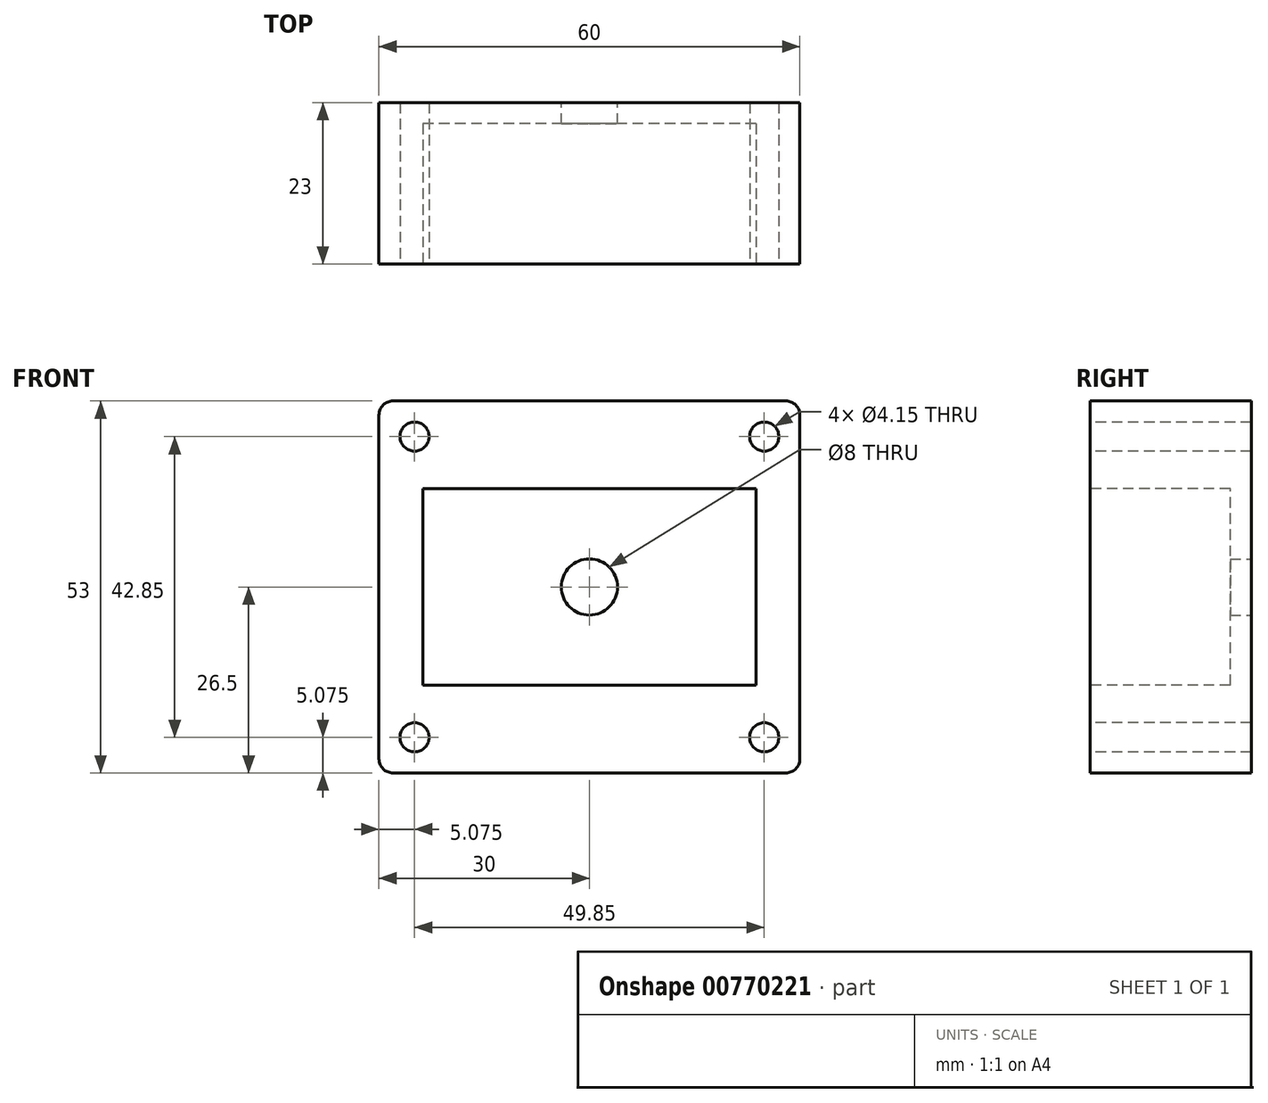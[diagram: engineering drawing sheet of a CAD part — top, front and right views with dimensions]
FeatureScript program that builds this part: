
annotation { "Feature Type Name" : "Feature", "Feature Type Description" : "" }
export const myFeature = defineFeature(function(context is Context, id is Id, definition is map)
    precondition{}
    {
        {
            var Q0;
            Q0=qCreatedBy(makeId("Front.planeOp"),FACE);
            var sketch = newSketch(context, id + "F0", { "sketchPlane" : qUnion([Q0])});
            skLineSegment(sketch, "E0.bottom", {"start": v(-30, 26.5) * mm, "end": v(30, 26.5) * mm});
            skLineSegment(sketch, "E0.top", {"start": v(-30, -26.5) * mm, "end": v(30, -26.5) * mm});
            skLineSegment(sketch, "E0.left", {"start": v(-30, 26.5) * mm, "end": v(-30, -26.5) * mm});
            skLineSegment(sketch, "E0.right", {"start": v(30, 26.5) * mm, "end": v(30, -26.5) * mm});
            skPoint(sketch, "E0.middle", {"position": v(0, 0) * mm});
            skSolve(sketch);
        }
        {
            var Q0;
            Q0=makeQuery(id+"F0.imprint","IMPRINT",FACE,{"disambiguationData":[TD([[makeQuery(id+"F0.imprint","IMPRINT",EDGE,{"derivedFrom":sQuery(id+"F0.wireOp",EDGE,"E0.bottom")}),-1.0]])]});
            extrude(context, id + "F1", {"entities" : qUnion([Q0]), "depth" : 23 * mm, "offsetDistance" : 25 * mm});
        }
        {
            var Q0;
            Q0=makeQuery(id+"F1.opExtrude","CAP_FACE",FACE,{"disambiguationData":[OSD([sQuery(id+"F0.wireOp",EDGE,"E0.bottom"),sQuery(id+"F0.wireOp",EDGE,"E0.top"),sQuery(id+"F0.wireOp",EDGE,"E0.left"),sQuery(id+"F0.wireOp",EDGE,"E0.right")])],"isStart":false});
            var sketch = newSketch(context, id + "F2", { "sketchPlane" : qUnion([Q0])});
            skLineSegment(sketch, "E1.bottom", {"start": v(23.75, -14) * mm, "end": v(-23.75, -14) * mm});
            skLineSegment(sketch, "E1.top", {"start": v(23.75, 14) * mm, "end": v(-23.75, 14) * mm});
            skLineSegment(sketch, "E1.left", {"start": v(23.75, -14) * mm, "end": v(23.75, 14) * mm});
            skLineSegment(sketch, "E1.right", {"start": v(-23.75, -14) * mm, "end": v(-23.75, 14) * mm});
            skPoint(sketch, "E1.middle", {"position": v(0, 0) * mm});
            skSolve(sketch);
        }
        {
            var Q0;
            Q0=makeQuery(id+"F2.imprint","IMPRINT",FACE,{"disambiguationData":[TD([[makeQuery(id+"F2.imprint","IMPRINT",EDGE,{"derivedFrom":sQuery(id+"F2.wireOp",EDGE,"E1.bottom")}),-1.0]])]});
            extrude(context, id + "F3", {"entities" : qUnion([Q0]), "operationType" : NewBodyOperationType.REMOVE, "depth" : -20 * mm, "offsetDistance" : 25 * mm});
        }
        {
            var Q0;
            Q0=makeQuery(id+"F1.opExtrude","SWEPT_EDGE",EDGE,{"disambiguationData":[OSD([sQuery(id+"F0.wireOp",EDGE,"E0.top"),sQuery(id+"F0.wireOp",EDGE,"E0.left")])]});
            fillet(context, id + "F4", {"entities" : qUnion([Q0]), "radius" : 2 * mm, "tangentPropagation" : true, "allowEdgeOverflow" : false});
        }
        {
            var Q0;
            Q0=makeQuery(id+"F1.opExtrude","SWEPT_EDGE",EDGE,{"disambiguationData":[OSD([sQuery(id+"F0.wireOp",EDGE,"E0.top"),sQuery(id+"F0.wireOp",EDGE,"E0.right")])]});
            var Q1;
            Q1=makeQuery(id+"F1.opExtrude","SWEPT_EDGE",EDGE,{"disambiguationData":[OSD([sQuery(id+"F0.wireOp",EDGE,"E0.bottom"),sQuery(id+"F0.wireOp",EDGE,"E0.right")])]});
            var Q2;
            Q2=makeQuery(id+"F1.opExtrude","SWEPT_EDGE",EDGE,{"disambiguationData":[OSD([sQuery(id+"F0.wireOp",EDGE,"E0.bottom"),sQuery(id+"F0.wireOp",EDGE,"E0.left")])]});
            fillet(context, id + "F5", {"entities" : qUnion([Q0, Q1, Q2]), "radius" : 2 * mm, "tangentPropagation" : true, "allowEdgeOverflow" : false});
        }
        {
            var Q0;
            Q0=makeQuery(id+"F1.opExtrude","CAP_FACE",FACE,{"disambiguationData":[OSD([sQuery(id+"F0.wireOp",EDGE,"E0.bottom"),sQuery(id+"F0.wireOp",EDGE,"E0.top"),sQuery(id+"F0.wireOp",EDGE,"E0.left"),sQuery(id+"F0.wireOp",EDGE,"E0.right")])],"isStart":true});
            var sketch = newSketch(context, id + "F6", { "sketchPlane" : qUnion([Q0])});
            skCircle(sketch, "E2", {"center": v(0, 0) * mm, "radius": 4 * mm});
            skSolve(sketch);
        }
        {
            var Q0;
            Q0=makeQuery(id+"F6.imprint","IMPRINT",FACE,{"disambiguationData":[TD([[makeQuery(id+"F6.imprint","IMPRINT",EDGE,{"derivedFrom":sQuery(id+"F6.wireOp",EDGE,"E2")}),1.0]])]});
            extrude(context, id + "F7", {"entities" : qUnion([Q0]), "operationType" : NewBodyOperationType.REMOVE, "oppositeDirection" : true, "depth" : 3 * mm, "offsetDistance" : 25 * mm});
        }
        {
            var Q0;
            Q0=makeQuery(id+"F1.opExtrude","CAP_FACE",FACE,{"disambiguationData":[OSD([sQuery(id+"F0.wireOp",EDGE,"E0.bottom"),sQuery(id+"F0.wireOp",EDGE,"E0.top"),sQuery(id+"F0.wireOp",EDGE,"E0.left"),sQuery(id+"F0.wireOp",EDGE,"E0.right")])],"isStart":false});
            var sketch = newSketch(context, id + "F8", { "sketchPlane" : qUnion([Q0])});
            skCircle(sketch, "E3", {"center": v(-24.92, 21.43) * mm, "radius": 2.08 * mm});
            skCircle(sketch, "E4", {"center": v(24.93, 21.43) * mm, "radius": 2.08 * mm});
            skCircle(sketch, "E5", {"center": v(24.92, -21.43) * mm, "radius": 2.08 * mm});
            skCircle(sketch, "E6", {"center": v(-24.93, -21.43) * mm, "radius": 2.08 * mm});
            skSolve(sketch);
        }
        {
            var Q0;
            Q0=makeQuery(id+"F8.imprint","IMPRINT",FACE,{"disambiguationData":[TD([[makeQuery(id+"F8.imprint","IMPRINT",EDGE,{"derivedFrom":sQuery(id+"F8.wireOp",EDGE,"E3")}),1.0]])]});
            var Q1;
            Q1=makeQuery(id+"F8.imprint","IMPRINT",FACE,{"disambiguationData":[TD([[makeQuery(id+"F8.imprint","IMPRINT",EDGE,{"derivedFrom":sQuery(id+"F8.wireOp",EDGE,"E4")}),1.0]])]});
            var Q2;
            Q2=makeQuery(id+"F8.imprint","IMPRINT",FACE,{"disambiguationData":[TD([[makeQuery(id+"F8.imprint","IMPRINT",EDGE,{"derivedFrom":sQuery(id+"F8.wireOp",EDGE,"E5")}),1.0]])]});
            var Q3;
            Q3=makeQuery(id+"F8.imprint","IMPRINT",FACE,{"disambiguationData":[TD([[makeQuery(id+"F8.imprint","IMPRINT",EDGE,{"derivedFrom":sQuery(id+"F8.wireOp",EDGE,"E6")}),1.0]])]});
            extrude(context, id + "F9", {"entities" : qUnion([Q0, Q1, Q2, Q3]), "operationType" : NewBodyOperationType.REMOVE, "oppositeDirection" : true, "depth" : 23 * mm, "offsetDistance" : 25 * mm});
        }
    });
